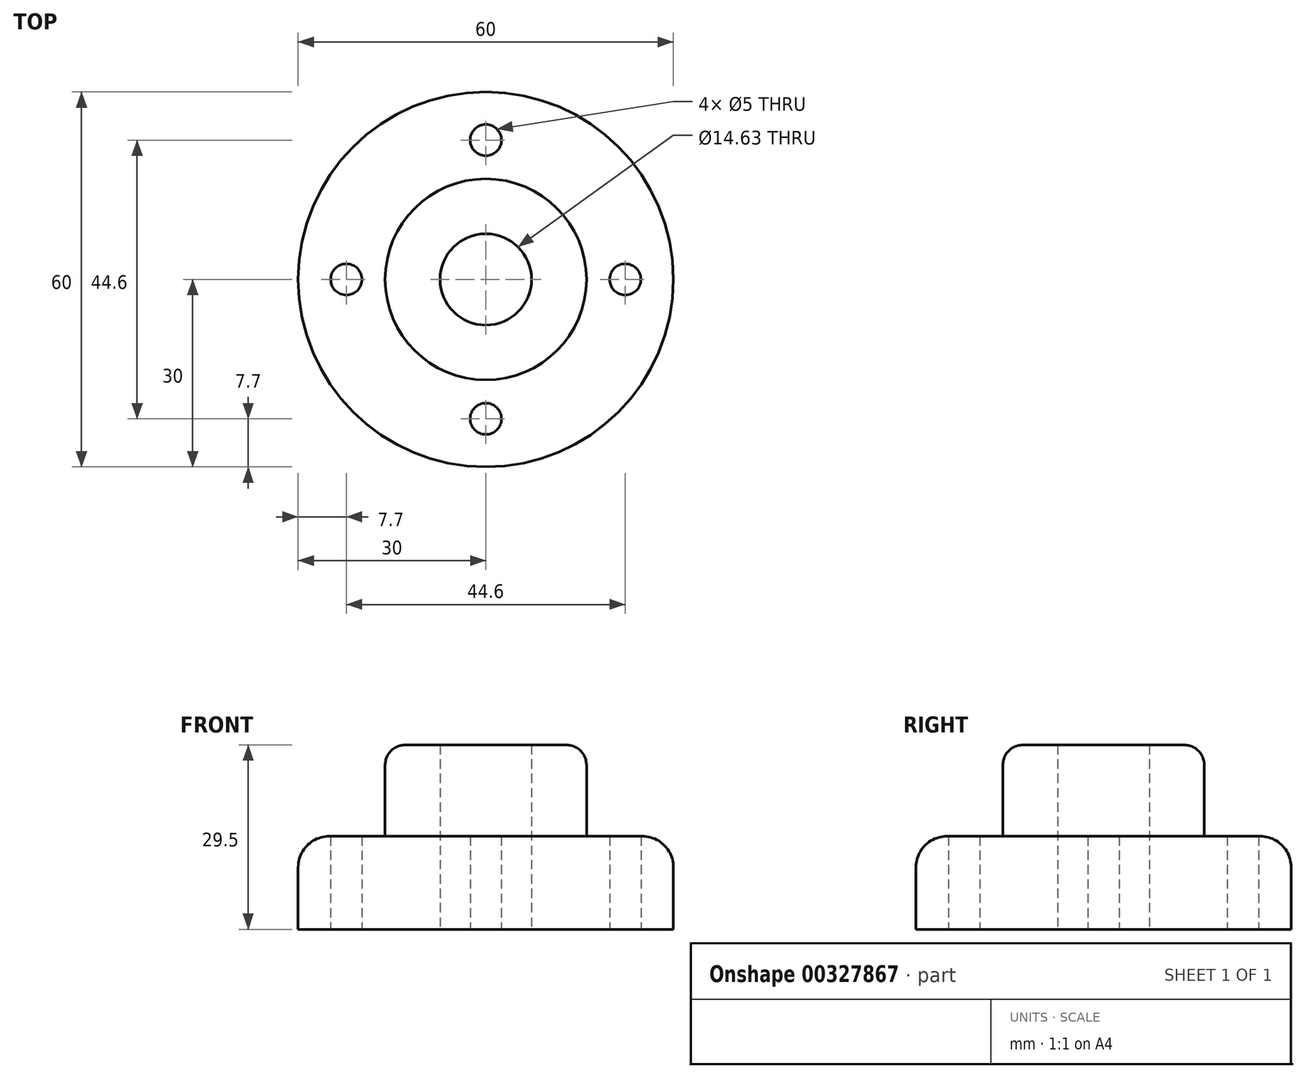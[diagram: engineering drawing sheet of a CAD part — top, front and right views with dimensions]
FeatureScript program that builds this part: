
annotation { "Feature Type Name" : "Feature", "Feature Type Description" : "" }
export const myFeature = defineFeature(function(context is Context, id is Id, definition is map)
    precondition{}
    {
        {
            var Q0;
            Q0=qCreatedBy(makeId("Top.planeOp"),FACE);
            var sketch = newSketch(context, id + "F0", { "sketchPlane" : qUnion([Q0])});
            skCircle(sketch, "E0", {"center": v(0, 0) * mm, "radius": 30 * mm});
            skCircle(sketch, "E1", {"center": v(0, 0) * mm, "radius": 16.1 * mm});
            skCircle(sketch, "E2", {"center": v(0, 0) * mm, "radius": 7.32 * mm});
            skCircle(sketch, "E3", {"center": v(-22.3, 0) * mm, "radius": 2.5 * mm});
            skCircle(sketch, "E4", {"center": v(22.3, 0) * mm, "radius": 2.5 * mm});
            skCircle(sketch, "E5", {"center": v(0, 22.3) * mm, "radius": 2.5 * mm});
            skCircle(sketch, "E6", {"center": v(0, -22.3) * mm, "radius": 2.5 * mm});
            skCircle(sketch, "E7", {"center": v(0, 0) * mm, "radius": 22.3 * mm});
            skSolve(sketch);
        }
        {
            var Q0;
            Q0=makeQuery(id+"F0.imprint","IMPRINT",FACE,{"disambiguationData":[TD([[makeQuery(id+"F0.imprint","IMPRINT",EDGE,{"derivedFrom":sQuery(id+"F0.wireOp",EDGE,"E0")}),1.0]])]});
            var Q1;
            Q1=makeQuery(id+"F0.imprint","IMPRINT",FACE,{"disambiguationData":[TD([[makeQuery(id+"F0.imprint","IMPRINT",EDGE,{"derivedFrom":sQuery(id+"F0.wireOp",EDGE,"E1")}),-1.0]])]});
            extrude(context, id + "F1", {"entities" : qUnion([Q0, Q1]), "depth" : 14.9 * mm});
        }
        {
            var Q0;
            Q0=makeQuery(id+"F0.imprint","IMPRINT",FACE,{"disambiguationData":[TD([[makeQuery(id+"F0.imprint","IMPRINT",EDGE,{"derivedFrom":sQuery(id+"F0.wireOp",EDGE,"E1")}),1.0]])]});
            extrude(context, id + "F2", {"entities" : qUnion([Q0]), "operationType" : NewBodyOperationType.ADD, "depth" : 29.5 * mm});
        }
        {
            var Q0;
            Q0=makeQuery(id+"F1.opExtrude","CAP_EDGE",EDGE,{"disambiguationData":[OSD([sQuery(id+"F0.wireOp",EDGE,"E0")])],"isStart":false});
            fillet(context, id + "F3", {"entities" : qUnion([Q0]), "radius" : 5 * mm, "tangentPropagation" : true, "allowEdgeOverflow" : false});
        }
        {
            var Q0;
            Q0=makeQuery(id+"F2.opExtrude","CAP_EDGE",EDGE,{"disambiguationData":[OSD([sQuery(id+"F0.wireOp",EDGE,"E1")])],"isStart":false});
            fillet(context, id + "F4", {"entities" : qUnion([Q0]), "radius" : 3.2 * mm, "tangentPropagation" : true, "allowEdgeOverflow" : false});
        }
    });
